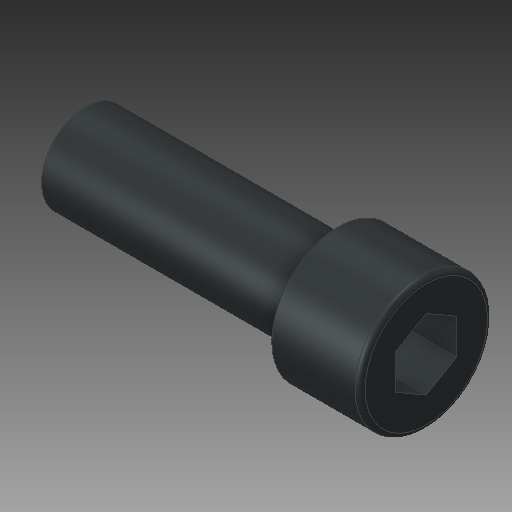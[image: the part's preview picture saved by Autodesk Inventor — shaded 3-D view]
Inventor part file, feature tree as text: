
AUTODESK INVENTOR PART (.ipt)
format: ipt  version: 2019 (Build 230136000, 136)  size: 135,680 bytes
history: native  units: mm
features: extrude x3, sketch x3, plane x1, fillet x1
ambient origin geometry x8: Origin, YZ Plane, XZ Plane, XY Plane, X Axis, Y Axis, Z Axis, Center Point
bodies: Solid1 (feature_tree)
feature tree (8):
  extrude  "Extrusion1"  Depth=10.0mm TaperAngle=0.0deg
  extrude  "Extrusion2"  Depth=3.5mm TaperAngle=0.0deg
  plane  "Work Plane1"
  extrude  "Extrusion3"  Depth=0.2mm
  fillet  "Fillet2"  Radius=1.75mm
  sketch  "Sketch1"  dims[d0=3.5mm d1=10.0mm d2=0.0mm]
  sketch  "Sketch2"  dims[d3=5.25mm d4=3.5mm d5=0.0mm]
  sketch  "Sketch3"  dims[d9=2.8mm d10=1.212436mm d11=1.75mm d12=0.0mm d13=0.2mm]
